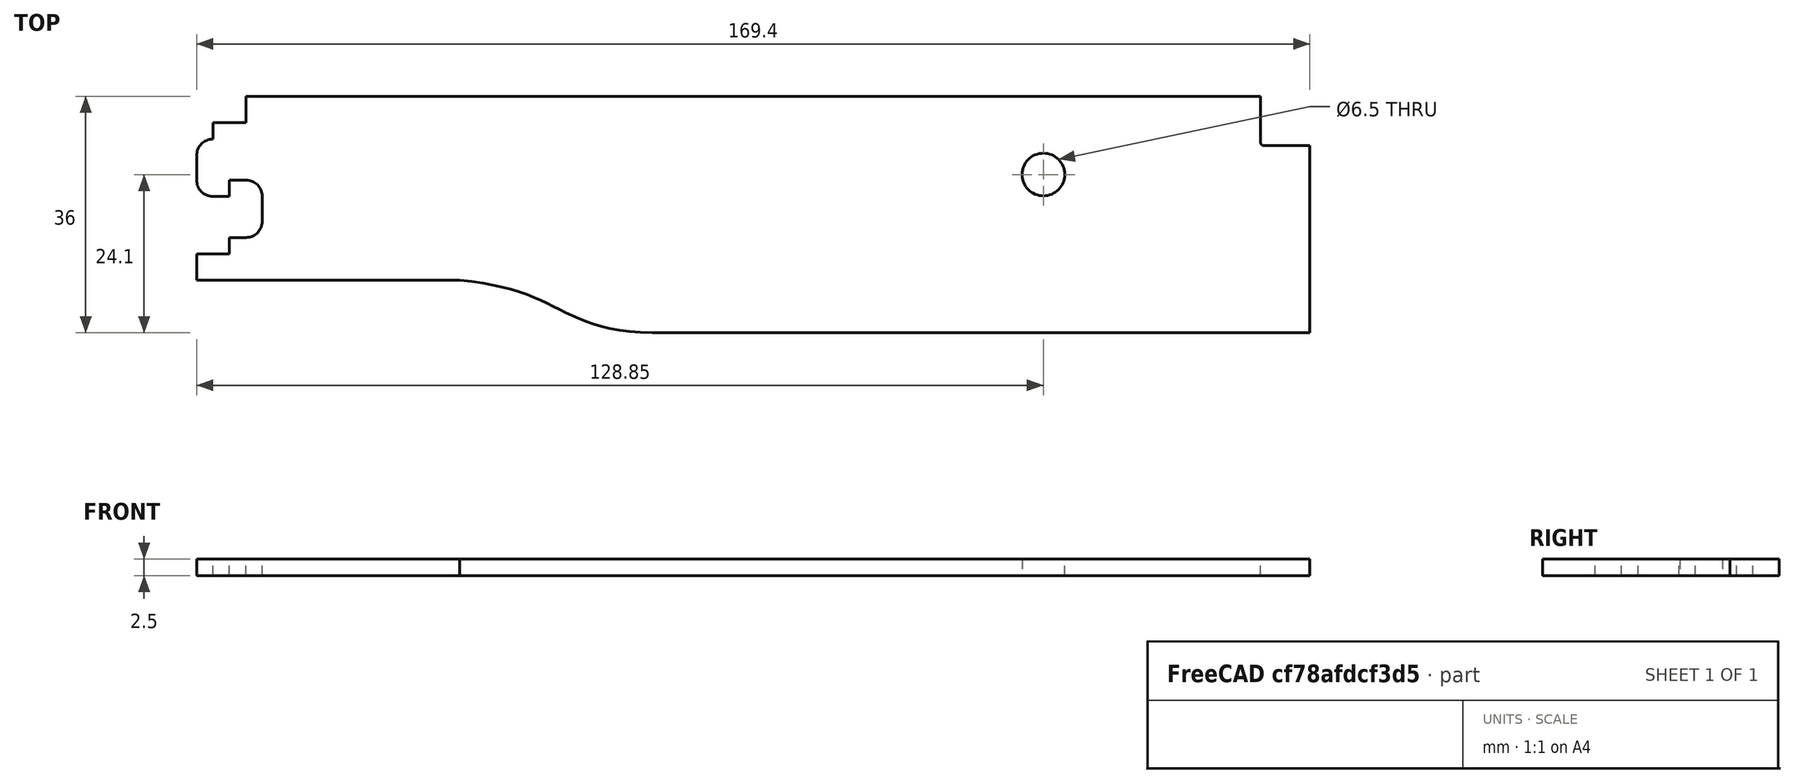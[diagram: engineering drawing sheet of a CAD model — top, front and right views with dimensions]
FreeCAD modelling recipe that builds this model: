
FCSTD DOCUMENT  (FreeCAD 0.19R0.19.2)
Label: v0_12
License: All rights reserved
LicenseURL: http://en.wikipedia.org/wiki/All_rights_reserved
objects: Sketcher::SketchObject×2, Part::Extrusion×1
note: 3 computed .brp shape members not serialized (recipe doc carries the construction recipe); baked Part::Feature solids carry a one-line shape summary decoded from their .brp

FEATURE [Sketcher::SketchObject] Sketch
  FullyConstrained = true
  sketch-geometry (33):
    g0: LineSegment StartX=0 StartY=0 StartZ=0 EndX=154.4 EndY=0 EndZ=0
    g1: LineSegment StartX=154.4 StartY=0 StartZ=0 EndX=154.4 EndY=-7 EndZ=0
    g2: LineSegment StartX=154.9 StartY=-7.5 StartZ=0 EndX=161.9 EndY=-7.5 EndZ=0
    g3: ArcOfCircle CenterX=154.9 CenterY=-7 CenterZ=0 NormalX=0 NormalY=0 NormalZ=1 AngleXU=0 Radius=0.5 StartAngle=3.14159 EndAngle=4.71239
    g4: Circle CenterX=121.35 CenterY=-11.9 CenterZ=0 NormalX=0 NormalY=0 NormalZ=1 AngleXU=0 Radius=3.25
    g5: LineSegment StartX=0 StartY=0 StartZ=0 EndX=0 EndY=-4 EndZ=0
    g6: LineSegment StartX=-5 StartY=-4 StartZ=0 EndX=0 EndY=-4 EndZ=0
    g7: LineSegment StartX=-5 StartY=-4 StartZ=0 EndX=-5 EndY=-6.5 EndZ=0
    g8: LineSegment StartX=-7.5 StartY=-9 StartZ=0 EndX=-7.5 EndY=-12.75 EndZ=0
    g9: ArcOfCircle CenterX=-5 CenterY=-9 CenterZ=0 NormalX=0 NormalY=0 NormalZ=1 AngleXU=0 Radius=2.5 StartAngle=1.5708 EndAngle=3.14159
    g10: LineSegment StartX=-5 StartY=-15.25 StartZ=0 EndX=-2.5 EndY=-15.25 EndZ=0
    g11: ArcOfCircle CenterX=-5 CenterY=-12.75 CenterZ=0 NormalX=0 NormalY=0 NormalZ=1 AngleXU=0 Radius=2.5 StartAngle=3.14159 EndAngle=4.71239
    g12: LineSegment StartX=-2.5 StartY=-15.25 StartZ=0 EndX=-2.5 EndY=-12.75 EndZ=0
    g13: LineSegment StartX=-2.5 StartY=-12.75 StartZ=0 EndX=1.488e-13 EndY=-12.75 EndZ=0
    g14: ArcOfCircle CenterX=1.486e-13 CenterY=-15.25 CenterZ=0 NormalX=0 NormalY=0 NormalZ=1 AngleXU=0 Radius=2.5 StartAngle=8e-16 EndAngle=1.5708
    g15: LineSegment StartX=2.5 StartY=-15.25 StartZ=0 EndX=2.5 EndY=-19 EndZ=0
    g16: ArcOfCircle CenterX=1.483e-13 CenterY=-19 CenterZ=0 NormalX=0 NormalY=0 NormalZ=1 AngleXU=0 Radius=2.5 StartAngle=4.71239 EndAngle=6.28319
    g17: LineSegment StartX=-2.5 StartY=-21.5 StartZ=0 EndX=1.479e-13 EndY=-21.5 EndZ=0
    g18: LineSegment StartX=-2.5 StartY=-21.5 StartZ=0 EndX=-2.5 EndY=-24 EndZ=0
    g19: LineSegment StartX=-7.5 StartY=-24 StartZ=0 EndX=-2.5 EndY=-24 EndZ=0
    g20: LineSegment StartX=-7.5 StartY=-24 StartZ=0 EndX=-7.5 EndY=-28 EndZ=0
    g21: LineSegment StartX=161.9 StartY=-7.5 StartZ=0 EndX=161.9 EndY=-36 EndZ=0
    g22: LineSegment StartX=61.85 StartY=-36 StartZ=0 EndX=161.9 EndY=-36 EndZ=0
    g23-g27: Circle x5 (B-spline internal-alignment scaffolding for g28; pole/knot coordinates omitted)
    g28: BSplineCurve PolesCount=5 KnotsCount=3 Degree=3 IsPeriodic=0
    g29: GeomPoint X=61.85 Y=-36 Z=0
    g30: GeomPoint X=47.2264 Y=-32.2128 Z=0
    g31: GeomPoint X=32.5209 Y=-28 Z=0
    g32: LineSegment StartX=32.5209 StartY=-28 StartZ=0 EndX=-7.5 EndY=-28 EndZ=0
  constraints (75):
    c: PointOnObject(g0,g-2)
    c: Horizontal(g0)
    c: Distance(g0) = 154.4
    c: DistanceY(g-1,g0) = 0
    c: Vertical(g1)
    c: Distance(g1) = 7
    c: Coincident(g1,g0)
    c: Horizontal(g2)
    c: Distance(g2) = 7
    c: Coincident(g3,g1)
    c: Tangent(g2,g3)
    c: Tangent(g2,g3,g2) = -1.5708
    c: Block(g3)
    c: Block(g4)
    c: Vertical(g5)
    c: Distance(g5) = 4
    c: Coincident(g5,g0)
    c: Horizontal(g6)
    c: Distance(g6) = 5
    c: Coincident(g6,g5)
    c: Vertical(g7)
    c: Distance(g7) = 2.5
    c: Coincident(g7,g6)
    c: Vertical(g8)
    c: Distance(g8) = 3.75
    c: Coincident(g9,g7)
    c: Block(g9)
    c: Coincident(g8,g9)
    c: Horizontal(g10)
    c: Distance(g10) = 2.5
    c: Coincident(g11,g8)
    c: Block(g11)
    c: Block(g10)
    c: Vertical(g12)
    c: Distance(g12) = 2.5
    c: Coincident(g12,g10)
    c: Horizontal(g13)
    c: Distance(g13) = 2.5
    c: Coincident(g13,g12)
    c: Coincident(g14,g13)
    c: Vertical(g15)
    c: Distance(g15) = 3.75
    c: Block(g14)
    c: Coincident(g15,g14)
    c: Coincident(g16,g15)
    c: Block(g16)
    c: Horizontal(g17)
    c: Distance(g17) = 2.5
    c: Coincident(g17,g16)
    c: Vertical(g18)
    c: Distance(g18) = 2.5
    c: Coincident(g18,g17)
    c: Horizontal(g19)
    c: Distance(g19) = 5
    c: Coincident(g19,g18)
    c: Vertical(g20)
    c: Distance(g20) = 4
    c: Coincident(g20,g19)
    c: Vertical(g21)
    c: Distance(g21) = 28.5
    c: Coincident(g21,g2)
    c: Horizontal(g22)
    c: Distance(g22) = 100.05
    c: Coincident(g22,g21)
    c: Coincident(g28,g22)
    c: Weight(g23) = 1
    c: Equal(g23, g24-g27) x4
    c: InternalAlignment(g23-g27 -> g28) x5
    c: InternalAlignment(g29,g28)
    c: InternalAlignment(g30,g28)
    c: InternalAlignment(g31,g28)
    c: Horizontal(g32)
    c: Coincident(g32,g20)
    c: Coincident(g32,g28)
    c: Block(g28)
FEATURE [Part::Extrusion] Extrude
  Base = -> Sketch
  Dir = (0,0,1)
  DirMode = 2
  FaceMakerClass = Part::FaceMakerBullseye
  LengthFwd = 2.5
  LengthRev = 0
  Solid = true
  Symmetric = false
FEATURE [Sketcher::SketchObject] Sketch001
  FullyConstrained = true
  sketch-geometry (58):
    g0: LineSegment StartX=0 StartY=0 StartZ=0 EndX=154.4 EndY=0 EndZ=0
    g1: LineSegment StartX=154.9 StartY=-7.5 StartZ=0 EndX=161.9 EndY=-7.5 EndZ=0
    g2: ArcOfCircle CenterX=154.9 CenterY=-7 CenterZ=0 NormalX=0 NormalY=0 NormalZ=1 AngleXU=0 Radius=0.5 StartAngle=3.14159 EndAngle=4.71239
    g3: LineSegment StartX=0 StartY=0 StartZ=0 EndX=0 EndY=-4 EndZ=0
    g4: LineSegment StartX=-5 StartY=-4 StartZ=0 EndX=0 EndY=-4 EndZ=0
    g5: LineSegment StartX=-5 StartY=-4 StartZ=0 EndX=-5 EndY=-6.5 EndZ=0
    g6: LineSegment StartX=-7.50066 StartY=-9 StartZ=0 EndX=-7.50066 EndY=-12.75 EndZ=0
    g7: ArcOfCircle CenterX=-5.00066 CenterY=-9 CenterZ=0 NormalX=0 NormalY=0 NormalZ=1 AngleXU=0 Radius=2.5 StartAngle=1.57053 EndAngle=3.14159
    g8: LineSegment StartX=-5 StartY=-15.25 StartZ=0 EndX=-2.5 EndY=-15.25 EndZ=0
    g9: ArcOfCircle CenterX=-5 CenterY=-12.75 CenterZ=0 NormalX=0 NormalY=0 NormalZ=1 AngleXU=0 Radius=2.50066 StartAngle=3.14159 EndAngle=4.71239
    g10: LineSegment StartX=-2.5 StartY=-15.25 StartZ=0 EndX=-2.5 EndY=-12.75 EndZ=0
    g11: LineSegment StartX=-2.5 StartY=-12.75 StartZ=0 EndX=1.488e-13 EndY=-12.75 EndZ=0
    g12: ArcOfCircle CenterX=1.486e-13 CenterY=-15.25 CenterZ=0 NormalX=0 NormalY=0 NormalZ=1 AngleXU=0 Radius=2.5 StartAngle=8e-16 EndAngle=1.5708
    g13: LineSegment StartX=2.5 StartY=-15.25 StartZ=0 EndX=2.5 EndY=-19 EndZ=0
    g14: ArcOfCircle CenterX=1.483e-13 CenterY=-19 CenterZ=0 NormalX=0 NormalY=0 NormalZ=1 AngleXU=0 Radius=2.5 StartAngle=4.71239 EndAngle=6.28319
    g15: LineSegment StartX=-2.5 StartY=-21.5 StartZ=0 EndX=1.812e-13 EndY=-21.5 EndZ=0
    g16: LineSegment StartX=-2.5 StartY=-21.5 StartZ=0 EndX=-2.5 EndY=-24 EndZ=0
    g17: LineSegment StartX=-7.5 StartY=-24 StartZ=0 EndX=-2.5 EndY=-24 EndZ=0
    g18: LineSegment StartX=-7.5 StartY=-24 StartZ=0 EndX=-7.5 EndY=-28 EndZ=0
    g19: LineSegment StartX=161.9 StartY=-7.5 StartZ=0 EndX=161.9 EndY=-36 EndZ=0
    g20: LineSegment StartX=61.85 StartY=-36 StartZ=0 EndX=161.9 EndY=-36 EndZ=0
    g21-g25: Circle x5 (B-spline internal-alignment scaffolding for g26; pole/knot coordinates omitted)
    g26: BSplineCurve PolesCount=5 KnotsCount=3 Degree=3 IsPeriodic=0
    g27: GeomPoint X=61.85 Y=-36 Z=0
    g28: GeomPoint X=47.2264 Y=-32.2128 Z=0
    g29: GeomPoint X=32.5209 Y=-28 Z=0
    g30: LineSegment StartX=154.4 StartY=0 StartZ=0 EndX=154.4 EndY=-3 EndZ=0
    g31: ArcOfCircle CenterX=154.9 CenterY=-7 CenterZ=0 NormalX=0 NormalY=0 NormalZ=1 AngleXU=0 Radius=3.5 StartAngle=3.14159 EndAngle=4.71239
    g32: LineSegment StartX=161.9 StartY=-7.5 StartZ=0 EndX=161.9 EndY=-10.5 EndZ=0
    g33: LineSegment StartX=154.9 StartY=-10.5 StartZ=0 EndX=158.4 EndY=-10.5 EndZ=0
    g34: ArcOfCircle CenterX=158.4 CenterY=-11 CenterZ=0 NormalX=0 NormalY=0 NormalZ=1 AngleXU=0 Radius=0.5 StartAngle=0 EndAngle=1.5708
    g35: LineSegment StartX=161.9 StartY=-36 StartZ=0 EndX=158.9 EndY=-36 EndZ=0
    g36: ArcOfCircle CenterX=158.4 CenterY=-32.5 CenterZ=0 NormalX=0 NormalY=0 NormalZ=1 AngleXU=0 Radius=0.5 StartAngle=4.71239 EndAngle=6.28319
    g37: LineSegment StartX=158.9 StartY=-11 StartZ=0 EndX=158.9 EndY=-32.5 EndZ=0
    g38: LineSegment StartX=61.85 StartY=-33 StartZ=0 EndX=158.4 EndY=-33 EndZ=0
    g39: LineSegment StartX=151.4 StartY=-7 StartZ=0 EndX=151.4 EndY=-3.5 EndZ=0
    g40: ArcOfCircle CenterX=150.9 CenterY=-3.5 CenterZ=0 NormalX=0 NormalY=0 NormalZ=1 AngleXU=0 Radius=0.5 StartAngle=-5.0484e-12 EndAngle=1.5708
    g41: LineSegment StartX=0 StartY=0 StartZ=0 EndX=5 EndY=0 EndZ=0
    g42: ArcOfCircle CenterX=8 CenterY=-6 CenterZ=0 NormalX=0 NormalY=0 NormalZ=1 AngleXU=0 Radius=3 StartAngle=1.5708 EndAngle=3.14159
    g43: LineSegment StartX=8 StartY=-3 StartZ=0 EndX=150.9 EndY=-3 EndZ=0
    g44: LineSegment StartX=154.4 StartY=-3 StartZ=0 EndX=154.4 EndY=-7 EndZ=0
    g45: LineSegment StartX=5 StartY=-6 StartZ=0 EndX=5 EndY=-22 EndZ=0
    g46: LineSegment StartX=-7.5 StartY=-28 StartZ=0 EndX=32.5209 EndY=-28 EndZ=0
    g47: ArcOfCircle CenterX=8 CenterY=-22 CenterZ=0 NormalX=0 NormalY=0 NormalZ=1 AngleXU=0 Radius=3 StartAngle=3.14159 EndAngle=4.71239
    g48: LineSegment StartX=8 StartY=-25 StartZ=0 EndX=32.52 EndY=-25 EndZ=0
    g49-g53: Circle x5 (B-spline internal-alignment scaffolding for g54; pole/knot coordinates omitted)
    g54: BSplineCurve PolesCount=5 KnotsCount=3 Degree=3 IsPeriodic=0
    g55: GeomPoint X=32.52 Y=-25 Z=0
    g56: GeomPoint X=47.2188 Y=-29.105 Z=0
    g57: GeomPoint X=61.85 Y=-33 Z=0
  constraints (124):
    c: PointOnObject(g0,g-2)
    c: Horizontal(g0)
    c: Distance(g0) = 154.4
    c: DistanceY(g-1,g0) = 0
    c: Horizontal(g1)
    c: Distance(g1) = 7
    c: Tangent(g1,g2)
    c: Tangent(g1,g2,g1) = -1.5708
    c: Block(g2)
    c: Vertical(g3)
    c: Distance(g3) = 4
    c: Coincident(g3,g0)
    c: Horizontal(g4)
    c: Distance(g4) = 5
    c: Coincident(g4,g3)
    c: Vertical(g5)
    c: Distance(g5) = 2.5
    c: Coincident(g5,g4)
    c: Vertical(g6)
    c: Distance(g6) = 3.75
    c: Coincident(g7,g5)
    c: Block(g7)
    c: Coincident(g6,g7)
    c: Horizontal(g8)
    c: Distance(g8) = 2.5
    c: Coincident(g9,g6)
    c: Block(g9)
    c: Block(g8)
    c: Vertical(g10)
    c: Distance(g10) = 2.5
    c: Coincident(g10,g8)
    c: Horizontal(g11)
    c: Distance(g11) = 2.5
    c: Coincident(g11,g10)
    c: Coincident(g12,g11)
    c: Vertical(g13)
    c: Distance(g13) = 3.75
    c: Block(g12)
    c: Coincident(g13,g12)
    c: Coincident(g14,g13)
    c: Block(g14)
    c: Horizontal(g15)
    c: Distance(g15) = 2.5
    c: Coincident(g15,g14)
    c: Vertical(g16)
    c: Distance(g16) = 2.5
    c: Coincident(g16,g15)
    c: Horizontal(g17)
    c: Distance(g17) = 5
    c: Coincident(g17,g16)
    c: Vertical(g18)
    c: Distance(g18) = 4
    c: Coincident(g18,g17)
    c: Vertical(g19)
    c: Distance(g19) = 28.5
    c: Coincident(g19,g1)
    c: Horizontal(g20)
    c: Distance(g20) = 100.05
    c: Coincident(g20,g19)
    c: Coincident(g26,g20)
    c: Weight(g21) = 1
    c: Equal(g21, g22-g25) x4
    c: InternalAlignment(g21-g25 -> g26) x5
    c: InternalAlignment(g27,g26)
    c: InternalAlignment(g28,g26)
    c: InternalAlignment(g29,g26)
    c: Block(g26)
    c: Vertical(g30)
    c: Distance(g30) = 3
    c: Coincident(g30,g0)
    c: Coincident(g31,g2)
    c: Vertical(g32)
    c: Distance(g32) = 3
    c: Coincident(g32,g1)
    c: Block(g31)
    c: Horizontal(g33)
    c: Distance(g33) = 3.5
    c: Coincident(g33,g31)
    c: Coincident(g34,g33)
    c: Block(g34)
    c: Horizontal(g35)
    c: Distance(g35) = 3
    c: Coincident(g35,g19)
    c: Block(g36)
    c: Vertical(g37)
    c: Coincident(g37,g36)
    c: Coincident(g37,g34)
    c: Horizontal(g38)
    c: Coincident(g38,g36)
    c: Distance(g38) = 96.55
    c: Vertical(g39)
    c: Distance(g39) = 3.5
    c: Coincident(g39,g31)
    c: Coincident(g40,g39)
    c: Block(g40)
    c: Horizontal(g41)
    c: Distance(g41) = 5
    c: Coincident(g41,g0)
    c: Block(g42)
    c: Horizontal(g43)
    c: Coincident(g43,g42)
    c: Coincident(g43,g40)
    c: Vertical(g44)
    c: Coincident(g44,g30)
    c: Coincident(g44,g2)
    c: Vertical(g45)
    c: Coincident(g45,g42)
    c: Horizontal(g46)
    c: Coincident(g46,g18)
    c: Coincident(g46,g26)
    c: Coincident(g47,g45)
    c: Block(g47)
    c: Horizontal(g48)
    c: Coincident(g48,g47)
    c: Distance(g48) = 24.52
    c: Coincident(g54,g48)
    c: Weight(g49) = 1
    c: Equal(g49, g50-g53) x4
    c: Coincident(g54,g38)
    c: InternalAlignment(g49-g53 -> g54) x5
    c: InternalAlignment(g55,g54)
    c: InternalAlignment(g56,g54)
    c: InternalAlignment(g57,g54)
    c: Block(g54)
